# Revit family: Скамейка стальная «Авиньон» без спинки Арт 15495
name_source: partatom
category: Антураж
revit_build: Autodesk Revit 2018 (Build: 20180423_1000(x64)
units: mm (PartAtom-declared; Revit-internal decimal feet)

## family parameters
Всегда вертикально = Да
Источник визуального образа = Геометрия семейства
На основе рабочей плоскости = Нет
Общий = Нет
При загрузке вырезать с полостями = Нет
Точка расчета площади = Нет

## types (2) — shared parameters
URL = https://hobbyka.ru
Артикул товара = Арт. 15495
Высота = 445 мм
Группа модели = Скамейки
Длина = 2250 мм
Изготовитель = ООО «Хоббика»
Изображение типоразмера = Скамейка стальная «Авиньон» без спинки Арт 15495.jpg
Материал изделия = Сталь, дерево
Цвет опоры = Сталь
Ширина = 460 мм

## per-type parameters (varying)
| type | Версия "Сосна" | Весия "Лиственница" | Описание | Цвет сидения |
| Версия "Сосна" | Да | Нет | Скамейка стальная «Авиньон» без спинки. Версия «Сосна» | Сосна |
| Версия "Лиственница" | Нет | Да | Скамейка стальная «Авиньон» без спинки. Версия «Лиственница» | Лиственница |
